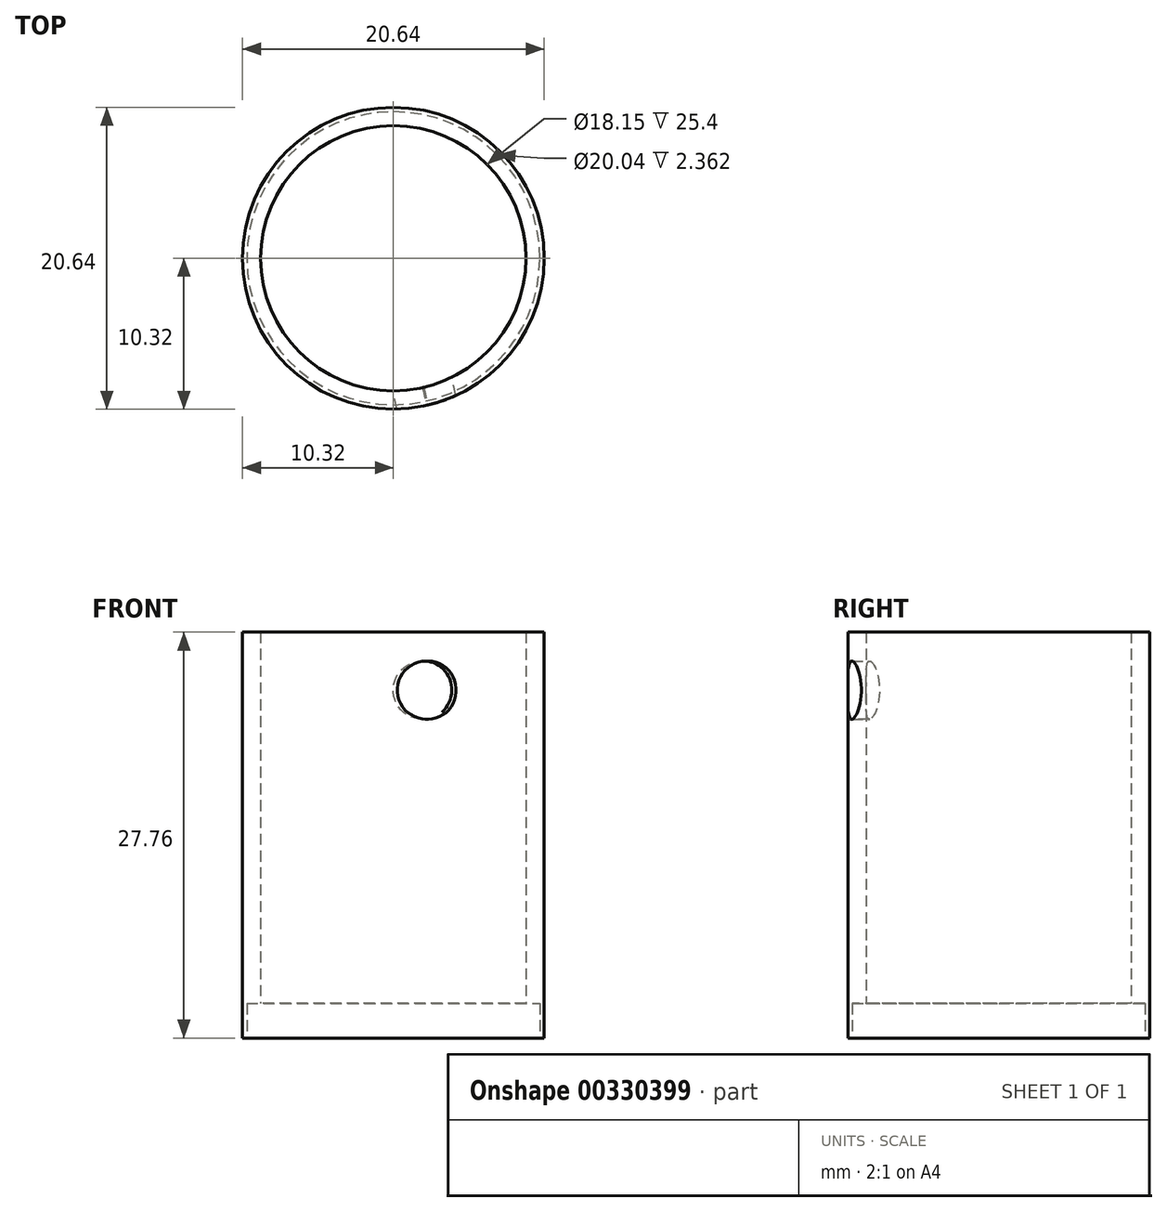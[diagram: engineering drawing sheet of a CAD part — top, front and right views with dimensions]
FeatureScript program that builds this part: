
annotation { "Feature Type Name" : "Feature", "Feature Type Description" : "" }
export const myFeature = defineFeature(function(context is Context, id is Id, definition is map)
    precondition{}
    {
        {
            var Q0;
            Q0=qCreatedBy(makeId("Top.planeOp"),FACE);
            var sketch = newSketch(context, id + "F0", { "sketchPlane" : qUnion([Q0])});
            skCircle(sketch, "E0", {"center": v(0, 0) * mm, "radius": 10.32 * mm});
            skSolve(sketch);
        }
        {
            var Q0;
            Q0 = qSketchRegion(id + "F0", true);
            extrude(context, id + "F1", {"entities" : qUnion([Q0]), "depth" : 27.76 * mm});
        }
        {
            var Q0;
            Q0=makeQuery(id+"F1.opExtrude","CAP_FACE",FACE,{"disambiguationData":[OSD([sQuery(id+"F0.wireOp",EDGE,"E0")])],"isStart":false});
            var Q1;
            Q1=makeQuery(id+"F1.opExtrude","CAP_FACE",FACE,{"disambiguationData":[OSD([sQuery(id+"F0.wireOp",EDGE,"E0")])],"isStart":true});
            shell(context, id + "F2", {"entities" : qUnion([Q0, Q1]), "thickness" : 1.24 * mm});
        }
        {
            var Q0;
            Q0=makeQuery(id+"F1.opExtrude","CAP_FACE",FACE,{"disambiguationData":[OSD([sQuery(id+"F0.wireOp",EDGE,"E0")])],"isStart":true});
            var sketch = newSketch(context, id + "F3", { "sketchPlane" : qUnion([Q0])});
            skCircle(sketch, "E1", {"center": v(0, 0) * mm, "radius": 10.02 * mm});
            skSolve(sketch);
        }
        {
            var Q0;
            Q0=makeQuery(id+"F3.imprint","IMPRINT",FACE,{"disambiguationData":[TD([[makeQuery(id+"F3.imprint","IMPRINT",EDGE,{"derivedFrom":sQuery(id+"F3.wireOp",EDGE,"E1")}),1.0]])]});
            extrude(context, id + "F4", {"entities" : qUnion([Q0]), "operationType" : NewBodyOperationType.REMOVE, "oppositeDirection" : true, "depth" : 2.36 * mm});
        }
        {
            var Q0;
            Q0=qCreatedBy(makeId("Right.planeOp"),FACE);
            var sketch = newSketch(context, id + "F5", { "sketchPlane" : qUnion([Q0])});
            skLineSegment(sketch, "E2", {"start": v(0, 0) * mm, "end": v(0, 52.54) * mm});
            skSolve(sketch);
        }
        {
            var Q0;
            Q0=qCreatedBy(makeId("Front.planeOp"),FACE);
            var Q1;
            Q1=sQuery(id+"F5.wireOp",EDGE,"E2");
            cPlane(context, id + "F6", {"entities" : qUnion([Q0, Q1]), "cplaneType" : CPlaneType.LINE_ANGLE, "offset" : 25.4 * mm, "angle" : 13 * degree, "width" : 152.4 * mm, "height" : 152.4 * mm});
        }
        {
            var Q0;
            Q0=qCreatedBy(makeId("Front.planeOp"),FACE);
            var Q1;
            Q1=sQuery(id+"F5.wireOp",EDGE,"E2");
            cPlane(context, id + "F7", {"entities" : qUnion([Q0, Q1]), "cplaneType" : CPlaneType.LINE_ANGLE, "offset" : 25.4 * mm, "angle" : 13.5 * degree, "width" : 152.4 * mm, "height" : 152.4 * mm});
        }
        {
            var Q0;
            Q0=qCreatedBy(id+"F7.planeOp",FACE);
            var sketch = newSketch(context, id + "F8", { "sketchPlane" : qUnion([Q0])});
            skCircle(sketch, "E3", {"center": v(0, 23.8) * mm, "radius": 1.98 * mm});
            skSolve(sketch);
        }
        {
            var Q0;
            Q0=makeQuery(id+"F8.imprint","IMPRINT",FACE,{"disambiguationData":[TD([[makeQuery(id+"F8.imprint","IMPRINT",EDGE,{"derivedFrom":sQuery(id+"F8.wireOp",EDGE,"E3")}),1.0]])]});
            extrude(context, id + "F9", {"entities" : qUnion([Q0]), "operationType" : NewBodyOperationType.REMOVE, "endBound" : BoundingType.THROUGH_ALL, "oppositeDirection" : true, "depth" : 25.4 * mm});
        }
        {
            var Q0;
            Q0=qCreatedBy(id+"F6.planeOp",FACE);
            var sketch = newSketch(context, id + "F10", { "sketchPlane" : qUnion([Q0])});
            skCircle(sketch, "E4", {"center": v(0, 23.8) * mm, "radius": 1.98 * mm});
            skSolve(sketch);
        }
        {
            var Q0;
            Q0 = qSketchRegion(id + "F10", true);
            extrude(context, id + "F11", {"entities" : qUnion([Q0]), "operationType" : NewBodyOperationType.REMOVE, "endBound" : BoundingType.THROUGH_ALL, "oppositeDirection" : true, "depth" : 25.4 * mm});
        }
        {
            var Q0;
            Q0=qCreatedBy(makeId("Front.planeOp"),FACE);
            var Q1;
            Q1=sQuery(id+"F5.wireOp",EDGE,"E2");
            cPlane(context, id + "F12", {"entities" : qUnion([Q0, Q1]), "cplaneType" : CPlaneType.LINE_ANGLE, "offset" : 25.4 * mm, "angle" : 12.5 * degree, "width" : 152.4 * mm, "height" : 152.4 * mm});
        }
        {
            var Q0;
            Q0=qCreatedBy(id+"F12.planeOp",FACE);
            var sketch = newSketch(context, id + "F13", { "sketchPlane" : qUnion([Q0])});
            skCircle(sketch, "E5", {"center": v(0, 23.8) * mm, "radius": 1.98 * mm});
            skSolve(sketch);
        }
        {
            var Q0;
            Q0 = qSketchRegion(id + "F13", true);
            extrude(context, id + "F14", {"entities" : qUnion([Q0]), "operationType" : NewBodyOperationType.REMOVE, "endBound" : BoundingType.THROUGH_ALL, "oppositeDirection" : true, "depth" : 25.4 * mm});
        }
    });
